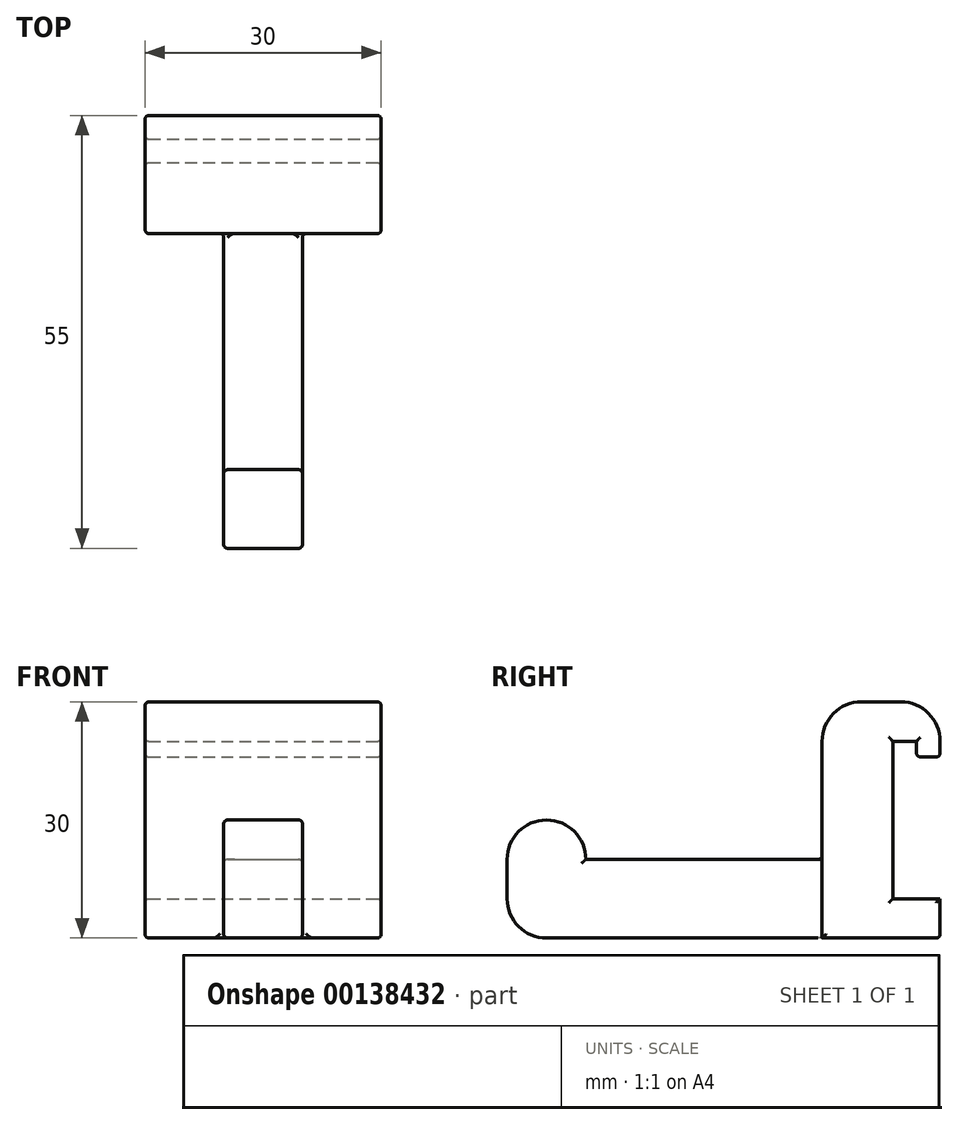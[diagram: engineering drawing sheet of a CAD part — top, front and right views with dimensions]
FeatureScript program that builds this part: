
annotation { "Feature Type Name" : "Feature", "Feature Type Description" : "" }
export const myFeature = defineFeature(function(context is Context, id is Id, definition is map)
    precondition{}
    {
        {
            var Q0;
            Q0=qCreatedBy(makeId("Front.planeOp"),FACE);
            var sketch = newSketch(context, id + "F0", { "sketchPlane" : qUnion([Q0])});
            skLineSegment(sketch, "E0.bottom", {"start": v(0, 0) * mm, "end": v(30, 0) * mm});
            skLineSegment(sketch, "E0.top", {"start": v(0, 30) * mm, "end": v(30, 30) * mm});
            skLineSegment(sketch, "E0.left", {"start": v(0, 0) * mm, "end": v(0, 30) * mm});
            skLineSegment(sketch, "E0.right", {"start": v(30, 0) * mm, "end": v(30, 30) * mm});
            skSolve(sketch);
        }
        {
            var Q0;
            Q0 = qSketchRegion(id + "F0", true);
            extrude(context, id + "F1", {"entities" : qUnion([Q0]), "depth" : 15 * mm});
        }
        {
            var Q0;
            Q0=makeQuery(id+"F1.opExtrude","SWEPT_FACE",FACE,{"disambiguationData":[OSD([sQuery(id+"F0.wireOp",EDGE,"E0.right")])]});
            var sketch = newSketch(context, id + "F2", { "sketchPlane" : qUnion([Q0])});
            skLineSegment(sketch, "E1", {"start": v(0, 5) * mm, "end": v(-6, 5) * mm});
            skLineSegment(sketch, "E2", {"start": v(-6, 5) * mm, "end": v(-6, 25) * mm});
            skLineSegment(sketch, "E3", {"start": v(-6, 25) * mm, "end": v(-3, 25) * mm});
            skLineSegment(sketch, "E4", {"start": v(-3, 25) * mm, "end": v(-3, 23) * mm});
            skLineSegment(sketch, "E5", {"start": v(-3, 23) * mm, "end": v(0, 23) * mm});
            skLineSegment(sketch, "E6", {"start": v(0, 23) * mm, "end": v(0, 5) * mm});
            skSolve(sketch);
        }
        {
            var Q0;
            Q0 = qSketchRegion(id + "F2", true);
            extrude(context, id + "F3", {"entities" : qUnion([Q0]), "operationType" : NewBodyOperationType.REMOVE, "endBound" : BoundingType.THROUGH_ALL, "oppositeDirection" : true, "depth" : 25 * mm});
        }
        {
            var Q0;
            Q0=makeQuery(id+"F1.opExtrude","CAP_FACE",FACE,{"disambiguationData":[OSD([sQuery(id+"F0.wireOp",EDGE,"E0.bottom"),sQuery(id+"F0.wireOp",EDGE,"E0.top"),sQuery(id+"F0.wireOp",EDGE,"E0.left"),sQuery(id+"F0.wireOp",EDGE,"E0.right")])],"isStart":false});
            var sketch = newSketch(context, id + "F4", { "sketchPlane" : qUnion([Q0])});
            skLineSegment(sketch, "E7.bottom", {"start": v(10, 0) * mm, "end": v(20, 0) * mm});
            skLineSegment(sketch, "E7.top", {"start": v(10, 10) * mm, "end": v(20, 10) * mm});
            skLineSegment(sketch, "E7.left", {"start": v(10, 0) * mm, "end": v(10, 10) * mm});
            skLineSegment(sketch, "E7.right", {"start": v(20, 0) * mm, "end": v(20, 10) * mm});
            skSolve(sketch);
        }
        {
            var Q0;
            Q0 = qSketchRegion(id + "F4", true);
            extrude(context, id + "F5", {"entities" : qUnion([Q0]), "operationType" : NewBodyOperationType.ADD, "depth" : 40 * mm});
        }
        {
            var Q0;
            Q0=makeQuery(id+"F5.opExtrude","SWEPT_FACE",FACE,{"disambiguationData":[OSD([sQuery(id+"F4.wireOp",EDGE,"E7.right")])]});
            var sketch = newSketch(context, id + "F6", { "sketchPlane" : qUnion([Q0])});
            skLineSegment(sketch, "E8.bottom", {"start": v(-55, 10) * mm, "end": v(-45, 10) * mm});
            skLineSegment(sketch, "E8.top", {"start": v(-55, 15) * mm, "end": v(-45, 15) * mm});
            skLineSegment(sketch, "E8.left", {"start": v(-55, 10) * mm, "end": v(-55, 15) * mm});
            skLineSegment(sketch, "E8.right", {"start": v(-45, 10) * mm, "end": v(-45, 15) * mm});
            skSolve(sketch);
        }
        {
            var Q0;
            Q0 = qSketchRegion(id + "F6", true);
            var Q1;
            Q1=makeQuery(id+"F5.opExtrude","SWEPT_FACE",FACE,{"disambiguationData":[OSD([sQuery(id+"F4.wireOp",EDGE,"E7.left")])]});
            extrude(context, id + "F7", {"entities" : qUnion([Q0]), "operationType" : NewBodyOperationType.ADD, "endBound" : BoundingType.UP_TO_SURFACE, "oppositeDirection" : true, "endBoundEntityFace" : qUnion([Q1]), "depth" : 25 * mm});
        }
        {
            var Q0;
            Q0=makeQuery(id+"F1.opExtrude","CAP_EDGE",EDGE,{"disambiguationData":[OSD([sQuery(id+"F0.wireOp",EDGE,"E0.top")])],"isStart":false});
            var Q1;
            Q1=makeQuery(id+"F1.opExtrude","CAP_EDGE",EDGE,{"disambiguationData":[OSD([sQuery(id+"F0.wireOp",EDGE,"E0.top")])],"isStart":true});
            var Q2;
            Q2=makeQuery(id+"F5.opExtrude","CAP_EDGE",EDGE,{"disambiguationData":[OSD([sQuery(id+"F4.wireOp",EDGE,"E7.top")])],"isStart":true});
            var Q3;
            Q3=makeQuery(id+"F5.opExtrude","CAP_EDGE",EDGE,{"disambiguationData":[OSD([sQuery(id+"F4.wireOp",EDGE,"E7.right")])],"isStart":true});
            var Q4;
            Q4=makeQuery(id+"F5.opExtrude","CAP_EDGE",EDGE,{"disambiguationData":[OSD([sQuery(id+"F4.wireOp",EDGE,"E7.left")])],"isStart":true});
            var Q5;
            Q5=makeQuery(id+"F7.opExtrude","SWEPT_EDGE",EDGE,{"disambiguationData":[OSD([sQuery(id+"F6.wireOp",EDGE,"E8.top"),sQuery(id+"F6.wireOp",EDGE,"E8.left")])]});
            var Q6;
            Q6=makeQuery(id+"F7.opExtrude","SWEPT_EDGE",EDGE,{"disambiguationData":[OSD([sQuery(id+"F6.wireOp",EDGE,"E8.top"),sQuery(id+"F6.wireOp",EDGE,"E8.right")])]});
            var Q7;
            Q7=makeQuery(id+"F5.opExtrude","CAP_EDGE",EDGE,{"disambiguationData":[OSD([sQuery(id+"F4.wireOp",EDGE,"E7.bottom")])],"isStart":false});
            fillet(context, id + "F8", {"entities" : qUnion([Q0, Q1, Q2, Q3, Q4, Q5, Q6, Q7]), "radius" : 5 * mm, "tangentPropagation" : true, "allowEdgeOverflow" : false});
        }
        {
            var Q0;
            Q0=makeQuery(id+"F1.opExtrude","SWEPT_FACE",FACE,{"disambiguationData":[OSD([sQuery(id+"F0.wireOp",EDGE,"E0.right")])]});
            var Q1;
            Q1=makeQuery(id+"F1.opExtrude","SWEPT_FACE",FACE,{"disambiguationData":[OSD([sQuery(id+"F0.wireOp",EDGE,"E0.left")])]});
            var Q2;
            Q2=makeQuery(id+"F7.boolean.opBoolean","MERGE",FACE,{"derivedFrom":[makeQuery(id+"F5.opExtrude","SWEPT_FACE",FACE,{"disambiguationData":[OSD([sQuery(id+"F4.wireOp",EDGE,"E7.right")])]}),makeQuery(id+"F7.opExtrude","CAP_FACE",FACE,{"disambiguationData":[OSD([sQuery(id+"F6.wireOp",EDGE,"E8.bottom"),sQuery(id+"F6.wireOp",EDGE,"E8.top"),sQuery(id+"F6.wireOp",EDGE,"E8.left"),sQuery(id+"F6.wireOp",EDGE,"E8.right")])],"isStart":true})]});
            var Q3;
            {var subQ0=sQuery(id+"F4.wireOp",EDGE,"E7.left");Q3=makeQuery(id+"F7.boolean.opBoolean","MERGE",FACE,{"derivedFrom":[makeQuery(id+"F5.opExtrude","SWEPT_FACE",FACE,{"disambiguationData":[OSD([subQ0])]}),makeQuery(id+"F7.opExtrude","CAP_FACE",FACE,{"disambiguationData":[OSD([subQ0])],"isStart":false})]});}
            var Q4;
            Q4=makeQuery(id+"F3.boolean.opBoolean","COPY",EDGE,{"derivedFrom":makeQuery(id+"F3.opExtrude","SWEPT_EDGE",EDGE,{"disambiguationData":[OSD([sQuery(id+"F0.wireOp",EDGE,"E0.right"),sQuery(id+"F2.wireOp",EDGE,"E1"),sQuery(id+"F2.wireOp",EDGE,"E6")])]})});
            var Q5;
            Q5=makeQuery(id+"F1.opExtrude","CAP_EDGE",EDGE,{"disambiguationData":[OSD([sQuery(id+"F0.wireOp",EDGE,"E0.bottom")])],"isStart":true});
            var Q6;
            Q6=makeQuery(id+"F3.boolean.opBoolean","COPY",EDGE,{"derivedFrom":makeQuery(id+"F3.opExtrude","SWEPT_EDGE",EDGE,{"disambiguationData":[OSD([sQuery(id+"F0.wireOp",EDGE,"E0.right"),sQuery(id+"F2.wireOp",EDGE,"E5"),sQuery(id+"F2.wireOp",EDGE,"E6")])]})});
            var Q7;
            Q7=makeQuery(id+"F3.boolean.opBoolean","COPY",EDGE,{"derivedFrom":makeQuery(id+"F3.opExtrude","SWEPT_EDGE",EDGE,{"disambiguationData":[OSD([sQuery(id+"F2.wireOp",EDGE,"E4"),sQuery(id+"F2.wireOp",EDGE,"E5")])]})});
            fillet(context, id + "F9", {"entities" : qUnion([Q0, Q1, Q2, Q3, Q4, Q5, Q6, Q7]), "radius" : 0.5 * mm, "tangentPropagation" : true, "allowEdgeOverflow" : false});
        }
    });
